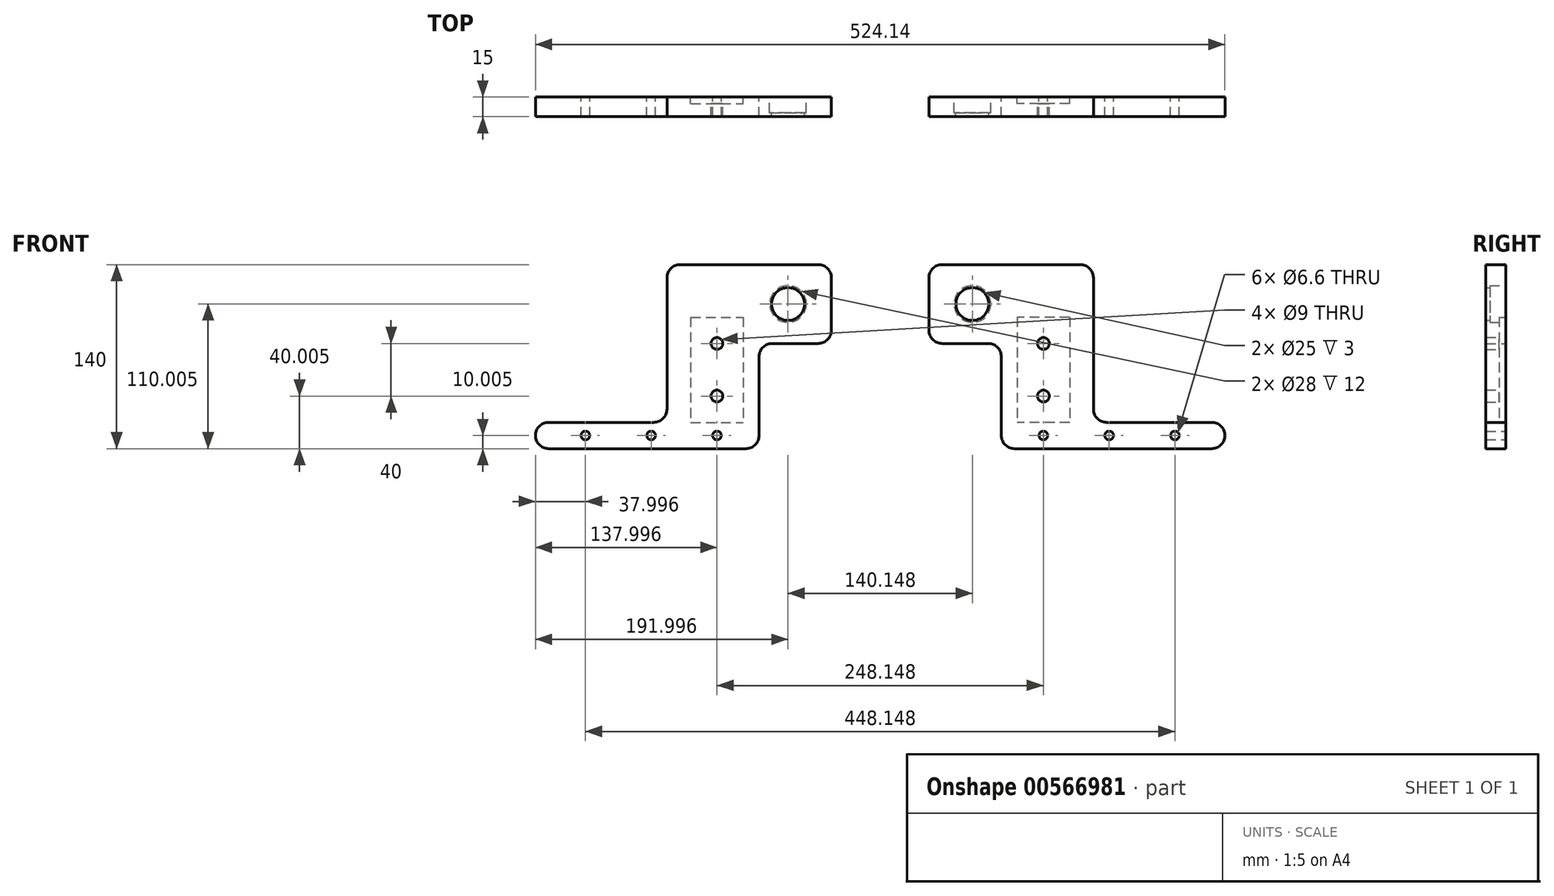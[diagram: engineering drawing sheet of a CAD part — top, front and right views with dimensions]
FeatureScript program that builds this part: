
annotation { "Feature Type Name" : "Feature", "Feature Type Description" : "" }
export const myFeature = defineFeature(function(context is Context, id is Id, definition is map)
    precondition{}
    {
        {
            var Q0;
            Q0=qCreatedBy(makeId("Front.planeOp"),FACE);
            var sketch = newSketch(context, id + "F0", { "sketchPlane" : qUnion([Q0])});
            skLineSegment(sketch, "E0", {"start": v(-57.93, 20.91) * mm, "end": v(62.07, 20.91) * mm});
            skLineSegment(sketch, "E1", {"start": v(62.07, 20.91) * mm, "end": v(62.07, -99.09) * mm});
            skLineSegment(sketch, "E2", {"start": v(62.07, -99.09) * mm, "end": v(162.07, -99.09) * mm});
            skLineSegment(sketch, "E3", {"start": v(162.07, -99.09) * mm, "end": v(162.07, -119.09) * mm});
            skLineSegment(sketch, "E4", {"start": v(162.07, -119.09) * mm, "end": v(-7.93, -119.09) * mm});
            skLineSegment(sketch, "E5", {"start": v(-7.93, -119.09) * mm, "end": v(-7.93, -39.09) * mm});
            skLineSegment(sketch, "E6", {"start": v(-7.93, -39.09) * mm, "end": v(-57.93, -39.09) * mm});
            skLineSegment(sketch, "E7", {"start": v(52.07, 10.91) * mm, "end": v(-47.93, 10.91) * mm, "construction": true});
            skLineSegment(sketch, "E8", {"start": v(-47.93, 10.91) * mm, "end": v(-47.93, -29.09) * mm, "construction": true});
            skLineSegment(sketch, "E9", {"start": v(-47.93, -29.09) * mm, "end": v(4.07, -29.09) * mm, "construction": true});
            skLineSegment(sketch, "E10", {"start": v(4.07, -29.09) * mm, "end": v(4.07, -119.09) * mm, "construction": true});
            skLineSegment(sketch, "E11", {"start": v(4.07, -119.09) * mm, "end": v(162.07, -119.09) * mm, "construction": true});
            skLineSegment(sketch, "E12", {"start": v(162.07, -119.09) * mm, "end": v(162.07, -99.09) * mm, "construction": true});
            skLineSegment(sketch, "E13", {"start": v(162.07, -99.09) * mm, "end": v(52.07, -99.09) * mm, "construction": true});
            skLineSegment(sketch, "E14", {"start": v(52.07, -99.09) * mm, "end": v(52.07, 10.91) * mm, "construction": true});
            skPoint(sketch, "E15", {"position": v(24.07, -109.09) * mm});
            skPoint(sketch, "E16", {"position": v(24.07, -79.09) * mm});
            skPoint(sketch, "E17", {"position": v(24.07, -39.09) * mm});
            skPoint(sketch, "E18", {"position": v(74.07, -109.09) * mm});
            skPoint(sketch, "E19", {"position": v(124.07, -109.09) * mm});
            skPoint(sketch, "E20", {"position": v(-29.93, -9.09) * mm});
            skPoint(sketch, "E21", {"position": v(-53.5, 14.48) * mm});
            skLineSegment(sketch, "E22", {"start": v(-44.33, -9.09) * mm, "end": v(-15.97, -9.09) * mm, "construction": true});
            skLineSegment(sketch, "E23", {"start": v(-29.93, 7.3) * mm, "end": v(-29.93, -21.44) * mm, "construction": true});
            skPoint(sketch, "E24.MirrorP", {"position": v(-53.5, -32.66) * mm});
            skPoint(sketch, "E25.MirrorP", {"position": v(-6.36, 14.48) * mm});
            skPoint(sketch, "E26.MirrorP", {"position": v(-6.36, -32.66) * mm});
            skLineSegment(sketch, "E27", {"start": v(-57.93, 20.91) * mm, "end": v(-62.93, 20.91) * mm});
            skLineSegment(sketch, "E28", {"start": v(-62.93, 20.91) * mm, "end": v(-62.93, -39.09) * mm});
            skLineSegment(sketch, "E29", {"start": v(-62.93, -39.09) * mm, "end": v(-57.93, -39.09) * mm});
            skSolve(sketch);
        }
        {
            var Q0;
            Q0=makeQuery(id+"F0.imprint","IMPRINT",FACE,{"disambiguationData":[TD([[makeQuery(id+"F0.imprint","IMPRINT",EDGE,{"derivedFrom":sQuery(id+"F0.wireOp",EDGE,"E0")}),-1.0]])]});
            extrude(context, id + "F1", {"entities" : qUnion([Q0]), "depth" : 15 * mm});
        }
        {
            var Q0;
            Q0=sQuery(id+"F0.wireOp",VERTEX,"E16");
            var Q1;
            Q1=sQuery(id+"F0.wireOp",VERTEX,"E17");
            var Q2;
            Q2=makeQuery(id+"F1.opExtrude","SWEPT_BODY",BODY,{"disambiguationData":[OSD([sQuery(id+"F0.wireOp",EDGE,"E0"),sQuery(id+"F0.wireOp",EDGE,"E1"),sQuery(id+"F0.wireOp",EDGE,"E2"),sQuery(id+"F0.wireOp",EDGE,"E3"),sQuery(id+"F0.wireOp",EDGE,"E4"),sQuery(id+"F0.wireOp",EDGE,"E5"),sQuery(id+"F0.wireOp",EDGE,"E6"),sQuery(id+"F0.wireOp",EDGE,"cvZF5QLb-uWAo-robz-iAHo-1Gj3ORty2Von")])]});
            hole(context, id + "F2", {"style" : HoleStyle.SIMPLE, "endStyle" : HoleEndStyle.THROUGH, "oppositeDirection" : true, "holeDiameter" : 9 * mm, "locations" : qUnion([Q0, Q1]), "scope" : qUnion([Q2]), "tappedDepth" : 12 * mm, "tapClearance" : 3});
        }
        {
            var Q0;
            Q0=sQuery(id+"F0.wireOp",VERTEX,"E15");
            var Q1;
            Q1=sQuery(id+"F0.wireOp",VERTEX,"E18");
            var Q2;
            Q2=sQuery(id+"F0.wireOp",VERTEX,"E19");
            var Q3;
            Q3=makeQuery(id+"F1.opExtrude","SWEPT_BODY",BODY,{"disambiguationData":[OSD([sQuery(id+"F0.wireOp",EDGE,"E0"),sQuery(id+"F0.wireOp",EDGE,"E1"),sQuery(id+"F0.wireOp",EDGE,"E2"),sQuery(id+"F0.wireOp",EDGE,"E3"),sQuery(id+"F0.wireOp",EDGE,"E4"),sQuery(id+"F0.wireOp",EDGE,"E5"),sQuery(id+"F0.wireOp",EDGE,"E6"),sQuery(id+"F0.wireOp",EDGE,"cvZF5QLb-uWAo-robz-iAHo-1Gj3ORty2Von")])]});
            hole(context, id + "F3", {"style" : HoleStyle.SIMPLE, "endStyle" : HoleEndStyle.THROUGH, "oppositeDirection" : true, "standardTappedOrClearance" : lookupTablePath({ "standard" : "ISO", "fit" : "Normal", "size" : "M6", "type" : "Clearance" }), "standardBlindInLast" : lookupTablePath({ "fit" : "Standard", "standard" : "ISO", "size" : "M6", "type" : "Clearance" }), "holeDiameter" : 6.6 * mm, "locations" : qUnion([Q0, Q1, Q2]), "scope" : qUnion([Q3]), "tappedDepth" : 12 * mm, "tapClearance" : 3});
        }
        {
            var Q0;
            Q0=makeQuery(id+"F1.opExtrude","SWEPT_EDGE",EDGE,{"disambiguationData":[OSD([sQuery(id+"F0.wireOp",EDGE,"E0"),sQuery(id+"F0.wireOp",EDGE,"cvZF5QLb-uWAo-robz-iAHo-1Gj3ORty2Von")])]});
            var Q1;
            Q1=makeQuery(id+"F1.opExtrude","SWEPT_EDGE",EDGE,{"disambiguationData":[OSD([sQuery(id+"F0.wireOp",EDGE,"E1"),sQuery(id+"F0.wireOp",EDGE,"E2")])]});
            var Q2;
            Q2=makeQuery(id+"F1.opExtrude","SWEPT_EDGE",EDGE,{"disambiguationData":[OSD([sQuery(id+"F0.wireOp",EDGE,"E0"),sQuery(id+"F0.wireOp",EDGE,"E1")])]});
            var Q3;
            Q3=makeQuery(id+"F1.opExtrude","SWEPT_EDGE",EDGE,{"disambiguationData":[OSD([sQuery(id+"F0.wireOp",EDGE,"E3"),sQuery(id+"F0.wireOp",EDGE,"E4")])]});
            var Q4;
            Q4=makeQuery(id+"F1.opExtrude","SWEPT_EDGE",EDGE,{"disambiguationData":[OSD([sQuery(id+"F0.wireOp",EDGE,"E2"),sQuery(id+"F0.wireOp",EDGE,"E3")])]});
            var Q5;
            Q5=makeQuery(id+"F1.opExtrude","SWEPT_EDGE",EDGE,{"disambiguationData":[OSD([sQuery(id+"F0.wireOp",EDGE,"E4"),sQuery(id+"F0.wireOp",EDGE,"E5")])]});
            var Q6;
            Q6=makeQuery(id+"F1.opExtrude","SWEPT_EDGE",EDGE,{"disambiguationData":[OSD([sQuery(id+"F0.wireOp",EDGE,"E5"),sQuery(id+"F0.wireOp",EDGE,"E6")])]});
            var Q7;
            Q7=makeQuery(id+"F1.opExtrude","SWEPT_EDGE",EDGE,{"disambiguationData":[OSD([sQuery(id+"F0.wireOp",EDGE,"E6"),sQuery(id+"F0.wireOp",EDGE,"cvZF5QLb-uWAo-robz-iAHo-1Gj3ORty2Von")])]});
            var Q8;
            Q8=makeQuery(id+"F1.opExtrude","SWEPT_EDGE",EDGE,{"disambiguationData":[OSD([sQuery(id+"F0.wireOp",EDGE,"E27"),sQuery(id+"F0.wireOp",EDGE,"E28")])]});
            var Q9;
            Q9=makeQuery(id+"F1.opExtrude","SWEPT_EDGE",EDGE,{"disambiguationData":[OSD([sQuery(id+"F0.wireOp",EDGE,"E28"),sQuery(id+"F0.wireOp",EDGE,"E29")])]});
            fillet(context, id + "F4", {"entities" : qUnion([Q0, Q1, Q2, Q3, Q4, Q5, Q6, Q7, Q8, Q9]), "radius" : 10 * mm, "tangentPropagation" : true, "allowEdgeOverflow" : false});
        }
        {
            var Q0;
            Q0=sQuery(id+"F0.wireOp",VERTEX,"E20");
            var Q1;
            Q1=makeQuery(id+"F1.opExtrude","SWEPT_BODY",BODY,{"disambiguationData":[OSD([sQuery(id+"F0.wireOp",EDGE,"E0"),sQuery(id+"F0.wireOp",EDGE,"E1"),sQuery(id+"F0.wireOp",EDGE,"E2"),sQuery(id+"F0.wireOp",EDGE,"E3"),sQuery(id+"F0.wireOp",EDGE,"E4"),sQuery(id+"F0.wireOp",EDGE,"E5"),sQuery(id+"F0.wireOp",EDGE,"E6"),sQuery(id+"F0.wireOp",EDGE,"cvZF5QLb-uWAo-robz-iAHo-1Gj3ORty2Von")])]});
            hole(context, id + "F5", {"style" : HoleStyle.C_BORE, "endStyle" : HoleEndStyle.THROUGH, "oppositeDirection" : true, "holeDiameter" : 25 * mm, "cBoreDiameter" : 28 * mm, "cBoreDepth" : 12 * mm, "locations" : qUnion([Q0]), "scope" : qUnion([Q1]), "tappedDepth" : 12 * mm, "tapClearance" : 3});
        }
        {
            var Q0;
            Q0=makeQuery(id+"F0.imprint","IMPRINT",FACE,{"disambiguationData":[TD([[makeQuery(id+"F0.imprint","IMPRINT",EDGE,{"derivedFrom":sQuery(id+"F0.wireOp",EDGE,"E0")}),-1.0]])]});
            var sketch = newSketch(context, id + "F6", { "sketchPlane" : qUnion([Q0])});
            skLineSegment(sketch, "E30.bottom", {"start": v(44.07, -19.09) * mm, "end": v(4.07, -19.09) * mm});
            skLineSegment(sketch, "E30.top", {"start": v(44.07, -99.09) * mm, "end": v(4.07, -99.09) * mm});
            skLineSegment(sketch, "E30.left", {"start": v(44.07, -19.09) * mm, "end": v(44.07, -99.09) * mm});
            skLineSegment(sketch, "E30.right", {"start": v(4.07, -19.09) * mm, "end": v(4.07, -99.09) * mm});
            skSolve(sketch);
        }
        {
            var Q0;
            Q0=qSketchRegion(id+"F6",true);
            extrude(context, id + "F7", {"entities" : qUnion([Q0]), "operationType" : NewBodyOperationType.REMOVE, "depth" : 5 * mm});
        }
        {
            var Q0;
            Q0=qCreatedBy(makeId("Right.planeOp"),FACE);
            cPlane(context, id + "F8", {"entities" : qUnion([Q0]), "cplaneType" : CPlaneType.OFFSET, "offset" : 100 * mm, "oppositeDirection" : true, "width" : 150 * mm, "height" : 150 * mm});
        }
        {
            var Q0;
            Q0=makeQuery(id+"F1.opExtrude","SWEPT_BODY",BODY,{"disambiguationData":[OSD([sQuery(id+"F0.wireOp",EDGE,"E0"),sQuery(id+"F0.wireOp",EDGE,"E1"),sQuery(id+"F0.wireOp",EDGE,"E2"),sQuery(id+"F0.wireOp",EDGE,"E3"),sQuery(id+"F0.wireOp",EDGE,"E4"),sQuery(id+"F0.wireOp",EDGE,"E5"),sQuery(id+"F0.wireOp",EDGE,"E6"),sQuery(id+"F0.wireOp",EDGE,"E27"),sQuery(id+"F0.wireOp",EDGE,"E28"),sQuery(id+"F0.wireOp",EDGE,"E29")])]});
            var Q1;
            Q1=qCreatedBy(id+"F8.planeOp",FACE);
            mirror(context, id + "F9", {"entities" : qUnion([Q0]), "mirrorPlane" : qUnion([Q1])});
        }
    });
